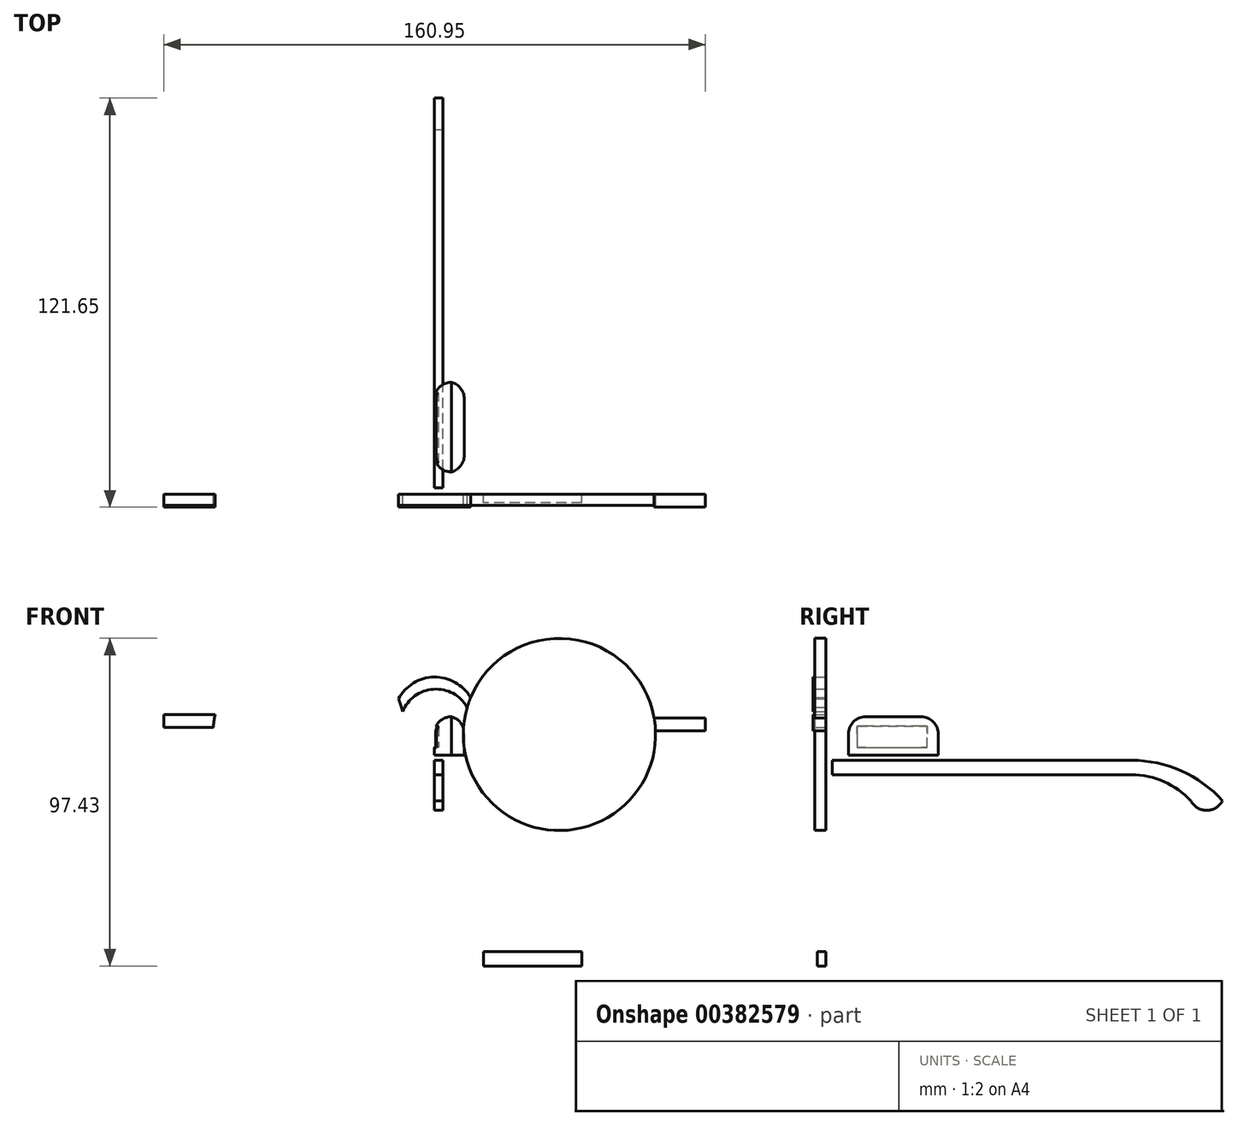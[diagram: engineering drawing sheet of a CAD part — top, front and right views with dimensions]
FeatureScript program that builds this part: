
annotation { "Feature Type Name" : "Feature", "Feature Type Description" : "" }
export const myFeature = defineFeature(function(context is Context, id is Id, definition is map)
    precondition{}
    {
        {
            var Q0;
            Q0=qCreatedBy(makeId("Front.planeOp"),FACE);
            var sketch = newSketch(context, id + "F0", { "sketchPlane" : qUnion([Q0])});
            skCircle(sketch, "E0", {"center": v(37.18, 36.55) * mm, "radius": 28.58 * mm});
            skCircle(sketch, "E1.MirrorC", {"center": v(-37.18, 36.55) * mm, "radius": 28.58 * mm});
            skLineSegment(sketch, "E2", {"start": v(-65.15, 42.41) * mm, "end": v(-80.39, 42.41) * mm});
            skLineSegment(sketch, "E3", {"start": v(-80.39, 42.41) * mm, "end": v(-80.39, 38.6) * mm});
            skLineSegment(sketch, "E4", {"start": v(-80.39, 38.6) * mm, "end": v(-65.68, 38.6) * mm});
            skLineSegment(sketch, "E5", {"start": v(65.32, 41.5) * mm, "end": v(80.56, 41.5) * mm});
            skLineSegment(sketch, "E6", {"start": v(80.56, 41.5) * mm, "end": v(80.56, 37.7) * mm});
            skLineSegment(sketch, "E7", {"start": v(80.56, 37.7) * mm, "end": v(65.73, 37.7) * mm});
            skArc(sketch, "E8", {"start": v(10.79, 47.5) * mm, "mid": v(-0.04, 53.61) * mm, "end": v(-10.63, 47.11) * mm});
            skArc(sketch, "E9", {"start": v(9.77, 44.63) * mm, "mid": v(-0.24, 50.01) * mm, "end": v(-9.42, 43.3) * mm});
            skSolve(sketch);
        }
        {
            var Q0;
            {var subQ0=sQuery(id+"F0.wireOp",EDGE,"E1.MirrorC");var subQ1=makeQuery(id+"F0.imprint","INTERSECT",VERTEX,{"derivedFrom":[subQ0,sQuery(id+"F0.wireOp",EDGE,"pmQuxhXs-luJx-pBtV-7lMD-aooJZGNjJs7K")]});Q0=makeQuery(id+"F0.imprint","IMPRINT",FACE,{"disambiguationData":[TD([[makeQuery(id+"F0.imprint","IMPRINT",EDGE,{"disambiguationData":[TD([[subQ1,1.0]])],"derivedFrom":subQ0}),-1.0]])]});}
            var Q1;
            {var subQ0=sQuery(id+"F0.wireOp",EDGE,"E0");var subQ1=makeQuery(id+"F0.imprint","INTERSECT",VERTEX,{"derivedFrom":[subQ0,sQuery(id+"F0.wireOp",EDGE,"pmQuxhXs-luJx-pBtV-7lMD-aooJZGNjJs7K")]});Q1=makeQuery(id+"F0.imprint","IMPRINT",FACE,{"disambiguationData":[TD([[makeQuery(id+"F0.imprint","IMPRINT",EDGE,{"disambiguationData":[TD([[subQ1,1.0]])],"derivedFrom":subQ0}),1.0]])]});}
            extrude(context, id + "F1", {"entities" : qUnion([Q0, Q1]), "depth" : 3.3 * mm});
        }
        {
            var Q0;
            Q0=qCreatedBy(makeId("Right.planeOp"),FACE);
            var sketch = newSketch(context, id + "F2", { "sketchPlane" : qUnion([Q0])});
            skLineSegment(sketch, "E10", {"start": v(1.93, 28.86) * mm, "end": v(1.93, 24.54) * mm});
            skLineSegment(sketch, "E11", {"start": v(1.93, 24.54) * mm, "end": v(90.83, 24.54) * mm});
            skLineSegment(sketch, "E12", {"start": v(1.93, 28.86) * mm, "end": v(90.83, 28.86) * mm});
            skArc(sketch, "E13", {"start": v(117.84, 16.81) * mm, "mid": v(105.62, 25.7) * mm, "end": v(90.83, 28.86) * mm});
            skArc(sketch, "E14", {"start": v(108.41, 16.81) * mm, "mid": v(100.43, 22.52) * mm, "end": v(90.83, 24.54) * mm});
            skArc(sketch, "E15", {"start": v(108.41, 16.81) * mm, "mid": v(113.13, 13.97) * mm, "end": v(117.84, 16.81) * mm});
            skSolve(sketch);
        }
        {
            var Q0;
            Q0=makeQuery(id+"F2.imprint","IMPRINT",FACE,{"disambiguationData":[TD([[makeQuery(id+"F2.imprint","IMPRINT",EDGE,{"derivedFrom":sQuery(id+"F2.wireOp",EDGE,"E10")}),1.0]])]});
            extrude(context, id + "F3", {"entities" : qUnion([Q0]), "depth" : 2.54 * mm});
        }
        {
            var Q0;
            Q0=qCreatedBy(makeId("Front.planeOp"),FACE);
            var sketch = newSketch(context, id + "F4", { "sketchPlane" : qUnion([Q0])});
            skLineSegment(sketch, "E16", {"start": v(43.8, -27.99) * mm, "end": v(14.58, -27.99) * mm});
            skLineSegment(sketch, "E17", {"start": v(43.8, -27.99) * mm, "end": v(43.8, -32.3) * mm});
            skLineSegment(sketch, "E18", {"start": v(14.58, -27.99) * mm, "end": v(14.58, -32.3) * mm});
            skLineSegment(sketch, "E19", {"start": v(43.8, -32.3) * mm, "end": v(14.58, -32.3) * mm});
            skSolve(sketch);
        }
        {
            var Q0;
            Q0=makeQuery(id+"F4.imprint","IMPRINT",FACE,{"disambiguationData":[TD([[makeQuery(id+"F4.imprint","IMPRINT",EDGE,{"derivedFrom":sQuery(id+"F4.wireOp",EDGE,"E16")}),1.0]])]});
            extrude(context, id + "F5", {"entities" : qUnion([Q0]), "depth" : 2.54 * mm});
        }
        {
            var Q0;
            {var subQ0=sQuery(id+"F0.wireOp",EDGE,"E2");Q0=makeQuery(id+"F0.imprint","IMPRINT",FACE,{"disambiguationData":[TD([[makeQuery(id+"F0.imprint","IMPRINT",EDGE,{"derivedFrom":subQ0}),1.0]])]});}
            var Q1;
            {var subQ0=sQuery(id+"F0.wireOp",EDGE,"E5");Q1=makeQuery(id+"F0.imprint","IMPRINT",FACE,{"disambiguationData":[TD([[makeQuery(id+"F0.imprint","IMPRINT",EDGE,{"derivedFrom":subQ0}),-1.0]])]});}
            extrude(context, id + "F6", {"entities" : qUnion([Q0, Q1]), "depth" : 3.8 * mm});
        }
        {
            var Q0;
            {var subQ0=sQuery(id+"F0.wireOp",EDGE,"E8");Q0=makeQuery(id+"F0.imprint","IMPRINT",FACE,{"disambiguationData":[TD([[makeQuery(id+"F0.imprint","IMPRINT",EDGE,{"derivedFrom":subQ0}),1.0]])]});}
            extrude(context, id + "F7", {"entities" : qUnion([Q0]), "depth" : 3.8 * mm});
        }
        {
            var Q0;
            Q0=qCreatedBy(makeId("Right.planeOp"),FACE);
            var sketch = newSketch(context, id + "F8", { "sketchPlane" : qUnion([Q0])});
            skLineSegment(sketch, "E20", {"start": v(6.68, 30.4) * mm, "end": v(33.35, 30.4) * mm});
            skLineSegment(sketch, "E21", {"start": v(33.35, 30.4) * mm, "end": v(33.35, 41.82) * mm});
            skLineSegment(sketch, "E22", {"start": v(6.68, 30.4) * mm, "end": v(6.68, 41.82) * mm});
            skLineSegment(sketch, "E23", {"start": v(6.68, 41.82) * mm, "end": v(33.35, 41.82) * mm});
            skSolve(sketch);
        }
        {
            var Q0;
            Q0=qCreatedBy(makeId("Right.planeOp"),FACE);
            var sketch = newSketch(context, id + "F9", { "sketchPlane" : qUnion([Q0])});
            skLineSegment(sketch, "E24", {"start": v(9.26, 38.99) * mm, "end": v(9.26, 32.64) * mm});
            skLineSegment(sketch, "E25", {"start": v(9.26, 32.64) * mm, "end": v(30.1, 32.64) * mm});
            skLineSegment(sketch, "E26", {"start": v(30.1, 32.64) * mm, "end": v(30.1, 38.99) * mm});
            skLineSegment(sketch, "E27", {"start": v(9.26, 38.99) * mm, "end": v(30.1, 38.99) * mm});
            skSolve(sketch);
        }
        {
            var Q0;
            Q0 = qSketchRegion(id + "F8", true);
            extrude(context, id + "F10", {"entities" : qUnion([Q0]), "depth" : 8.9 * mm});
        }
        {
            var Q0;
            Q0 = qSketchRegion(id + "F9", true);
            extrude(context, id + "F11", {"entities" : qUnion([Q0]), "operationType" : NewBodyOperationType.REMOVE, "depth" : 1.27 * mm});
        }
        {
            var Q0;
            Q0=makeQuery(id+"F10.opExtrude","CAP_EDGE",EDGE,{"disambiguationData":[OSD([sQuery(id+"F8.wireOp",EDGE,"E23")])],"isStart":true});
            fillet(context, id + "F12", {"entities" : qUnion([Q0]), "radius" : 5.08 * mm, "tangentPropagation" : true, "allowEdgeOverflow" : false});
        }
        {
            var Q0;
            Q0=makeQuery(id+"F10.opExtrude","CAP_EDGE",EDGE,{"disambiguationData":[OSD([sQuery(id+"F8.wireOp",EDGE,"E21")])],"isStart":true});
            var Q1;
            Q1=makeQuery(id+"F12.opFillet","BLEND_EDGE",EDGE,{"blendedFrom":[makeQuery(id+"F10.opExtrude","CAP_EDGE",EDGE,{"disambiguationData":[OSD([sQuery(id+"F8.wireOp",EDGE,"E23")])],"isStart":true}),makeQuery(id+"F10.opExtrude","SWEPT_FACE",FACE,{"disambiguationData":[OSD([sQuery(id+"F8.wireOp",EDGE,"E21")])]})],"blendedInto":[makeQuery(id+"F10.opExtrude","SWEPT_FACE",FACE,{"disambiguationData":[OSD([sQuery(id+"F8.wireOp",EDGE,"E21")])]})]});
            fillet(context, id + "F13", {"entities" : qUnion([Q0, Q1]), "radius" : 5.08 * mm, "tangentPropagation" : true, "allowEdgeOverflow" : false});
        }
        {
            var Q0;
            Q0=makeQuery(id+"F12.opFillet","BLEND_EDGE",EDGE,{"blendedFrom":[makeQuery(id+"F10.opExtrude","CAP_EDGE",EDGE,{"disambiguationData":[OSD([sQuery(id+"F8.wireOp",EDGE,"E23")])],"isStart":true}),makeQuery(id+"F10.opExtrude","SWEPT_FACE",FACE,{"disambiguationData":[OSD([sQuery(id+"F8.wireOp",EDGE,"E22")])]})],"blendedInto":[makeQuery(id+"F10.opExtrude","SWEPT_FACE",FACE,{"disambiguationData":[OSD([sQuery(id+"F8.wireOp",EDGE,"E22")])]})]});
            fillet(context, id + "F14", {"entities" : qUnion([Q0]), "radius" : 5.08 * mm, "tangentPropagation" : true, "allowEdgeOverflow" : false});
        }
        {
            var Q0;
            {var subQ0=sQuery(id+"F8.wireOp",EDGE,"E23");var subQ1=sQuery(id+"F8.wireOp",EDGE,"E21");Q0=makeQuery(id+"F13.opFillet","BLEND_EDGE",EDGE,{"blendedFrom":[makeQuery(id+"F10.opExtrude","SWEPT_EDGE",EDGE,{"disambiguationData":[OSD([subQ1,subQ0])]}),makeQuery(id+"F10.opExtrude","CAP_FACE",FACE,{"disambiguationData":[OSD([sQuery(id+"F8.wireOp",EDGE,"E20"),subQ1,sQuery(id+"F8.wireOp",EDGE,"E22"),subQ0])],"isStart":false})],"blendedInto":[makeQuery(id+"F10.opExtrude","CAP_FACE",FACE,{"disambiguationData":[OSD([sQuery(id+"F8.wireOp",EDGE,"E20"),subQ1,sQuery(id+"F8.wireOp",EDGE,"E22"),subQ0])],"isStart":false})]});}
            var Q1;
            Q1=makeQuery(id+"F10.opExtrude","CAP_EDGE",EDGE,{"disambiguationData":[OSD([sQuery(id+"F8.wireOp",EDGE,"E21")])],"isStart":false});
            fillet(context, id + "F15", {"entities" : qUnion([Q0, Q1]), "radius" : 5.08 * mm, "tangentPropagation" : true, "allowEdgeOverflow" : false});
        }
    });
